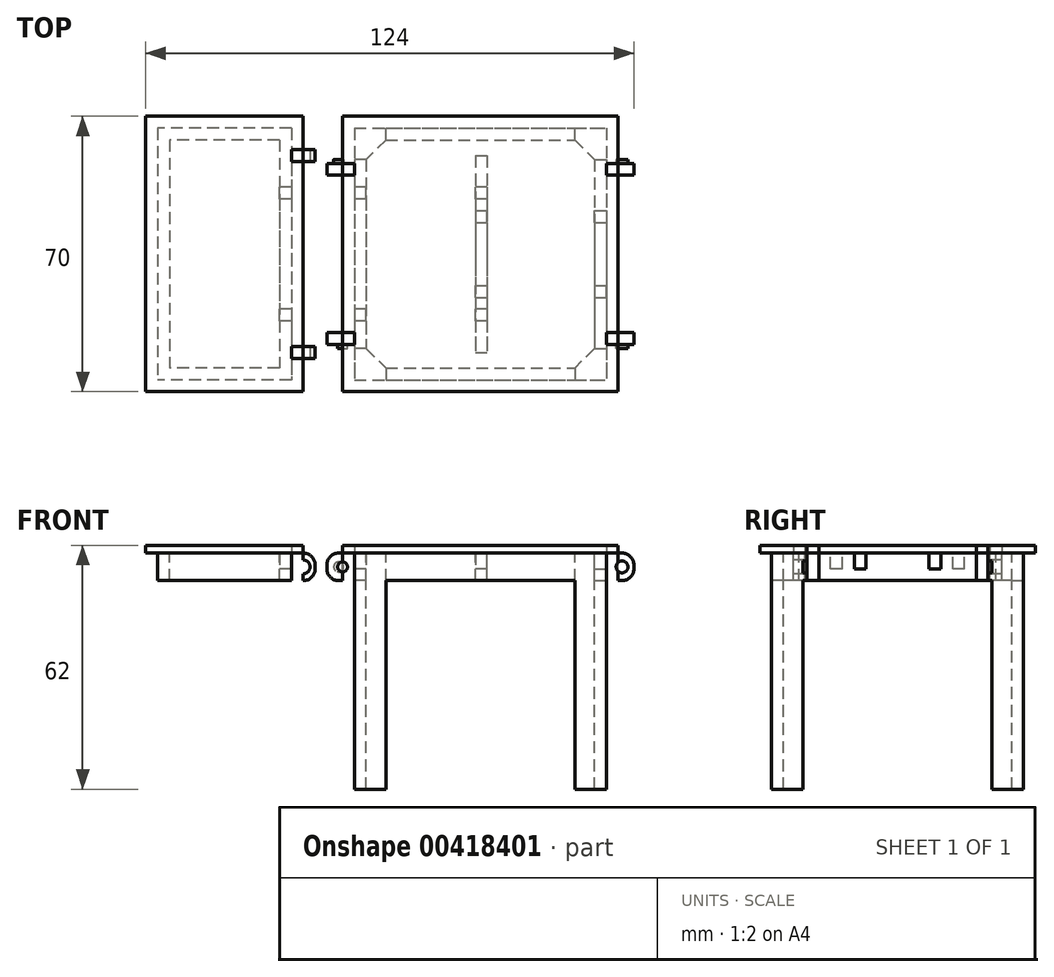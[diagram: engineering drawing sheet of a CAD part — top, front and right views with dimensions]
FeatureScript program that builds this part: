
annotation { "Feature Type Name" : "Feature", "Feature Type Description" : "" }
export const myFeature = defineFeature(function(context is Context, id is Id, definition is map)
    precondition{}
    {
        {
            var Q0;
            Q0=qCreatedBy(makeId("Top.planeOp"),FACE);
            var sketch = newSketch(context, id + "F0", { "sketchPlane" : qUnion([Q0])});
            skLineSegment(sketch, "E0.bottom", {"start": v(0, 0) * mm, "end": v(70, 0) * mm});
            skLineSegment(sketch, "E0.top", {"start": v(0, -70) * mm, "end": v(70, -70) * mm});
            skLineSegment(sketch, "E0.left", {"start": v(0, 0) * mm, "end": v(0, -70) * mm});
            skLineSegment(sketch, "E0.right", {"start": v(70, 0) * mm, "end": v(70, -70) * mm});
            skLineSegment(sketch, "E1.bottom", {"start": v(3, -3) * mm, "end": v(67, -3) * mm});
            skLineSegment(sketch, "E1.top", {"start": v(3, -67) * mm, "end": v(67, -67) * mm});
            skLineSegment(sketch, "E1.left", {"start": v(3, -3) * mm, "end": v(3, -67) * mm});
            skLineSegment(sketch, "E1.right", {"start": v(67, -3) * mm, "end": v(67, -67) * mm});
            skLineSegment(sketch, "E2.bottom", {"start": v(11, -6) * mm, "end": v(59, -6) * mm});
            skLineSegment(sketch, "E2.top", {"start": v(11, -64) * mm, "end": v(59, -64) * mm});
            skLineSegment(sketch, "E2.left", {"start": v(6, -11) * mm, "end": v(6, -59) * mm});
            skLineSegment(sketch, "E2.right", {"start": v(64, -11) * mm, "end": v(64, -59) * mm});
            skLineSegment(sketch, "E3", {"start": v(11, -6) * mm, "end": v(6, -11) * mm});
            skLineSegment(sketch, "E4", {"start": v(59, -6) * mm, "end": v(64, -11) * mm});
            skLineSegment(sketch, "E5", {"start": v(64, -59) * mm, "end": v(59, -64) * mm});
            skLineSegment(sketch, "E6", {"start": v(6, -59) * mm, "end": v(11, -64) * mm});
            skLineSegment(sketch, "E7", {"start": v(11, -6) * mm, "end": v(11, -3) * mm});
            skLineSegment(sketch, "E8", {"start": v(6, -11) * mm, "end": v(3, -11) * mm});
            skLineSegment(sketch, "E9", {"start": v(11, -64) * mm, "end": v(11, -67) * mm});
            skLineSegment(sketch, "E10", {"start": v(6, -59) * mm, "end": v(3, -59) * mm});
            skLineSegment(sketch, "E11", {"start": v(59, -64) * mm, "end": v(59, -67) * mm});
            skLineSegment(sketch, "E12", {"start": v(64, -59) * mm, "end": v(67, -59) * mm});
            skLineSegment(sketch, "E13", {"start": v(59, -6) * mm, "end": v(59, -3) * mm});
            skLineSegment(sketch, "E14", {"start": v(64, -11) * mm, "end": v(67, -11) * mm});
            skPoint(sketch, "E15.orphan", {"position": v(6, -6) * mm});
            skPoint(sketch, "E16.orphan", {"position": v(6, -64) * mm});
            skPoint(sketch, "E17.orphan", {"position": v(64, -64) * mm});
            skPoint(sketch, "E18.orphan", {"position": v(64, -6) * mm});
            skLineSegment(sketch, "E19.bottom", {"start": v(67, -12) * mm, "end": v(74, -12) * mm});
            skLineSegment(sketch, "E19.top", {"start": v(67, -15) * mm, "end": v(74, -15) * mm});
            skLineSegment(sketch, "E19.left", {"start": v(67, -12) * mm, "end": v(67, -15) * mm});
            skLineSegment(sketch, "E19.right", {"start": v(74, -12) * mm, "end": v(74, -15) * mm});
            skLineSegment(sketch, "E20.bottom", {"start": v(67, -58) * mm, "end": v(74, -58) * mm});
            skLineSegment(sketch, "E20.top", {"start": v(67, -55) * mm, "end": v(74, -55) * mm});
            skLineSegment(sketch, "E20.left", {"start": v(67, -58) * mm, "end": v(67, -55) * mm});
            skLineSegment(sketch, "E20.right", {"start": v(74, -58) * mm, "end": v(74, -55) * mm});
            skLineSegment(sketch, "E21.bottom", {"start": v(3, -12) * mm, "end": v(-4, -12) * mm});
            skLineSegment(sketch, "E21.top", {"start": v(3, -15) * mm, "end": v(-4, -15) * mm});
            skLineSegment(sketch, "E21.left", {"start": v(3, -12) * mm, "end": v(3, -15) * mm});
            skLineSegment(sketch, "E21.right", {"start": v(-4, -12) * mm, "end": v(-4, -15) * mm});
            skLineSegment(sketch, "E22.bottom", {"start": v(3, -58) * mm, "end": v(-4, -58) * mm});
            skLineSegment(sketch, "E22.top", {"start": v(3, -55) * mm, "end": v(-4, -55) * mm});
            skLineSegment(sketch, "E22.left", {"start": v(3, -58) * mm, "end": v(3, -55) * mm});
            skLineSegment(sketch, "E22.right", {"start": v(-4, -58) * mm, "end": v(-4, -55) * mm});
            skLineSegment(sketch, "E23.bottom", {"start": v(33.75, -10) * mm, "end": v(36.75, -10) * mm});
            skLineSegment(sketch, "E23.top", {"start": v(33.75, -60) * mm, "end": v(36.75, -60) * mm});
            skLineSegment(sketch, "E23.left", {"start": v(33.75, -10) * mm, "end": v(33.75, -60) * mm});
            skLineSegment(sketch, "E23.right", {"start": v(36.75, -10) * mm, "end": v(36.75, -60) * mm});
            skSolve(sketch);
        }
        {
            var Q0;
            Q0=makeQuery(id+"F0.imprint","IMPRINT",FACE,{"disambiguationData":[TD([[makeQuery(id+"F0.imprint","IMPRINT",EDGE,{"derivedFrom":sQuery(id+"F0.wireOp",EDGE,"E2.bottom")}),-1.0]])]});
            var Q1;
            Q1=makeQuery(id+"F0.imprint","IMPRINT",FACE,{"disambiguationData":[TD([[makeQuery(id+"F0.imprint","IMPRINT",EDGE,{"derivedFrom":sQuery(id+"F0.wireOp",EDGE,"E2.right")}),1.0]])]});
            var Q2;
            {var subQ14=sQuery(id+"F0.wireOp",EDGE,"E0.bottom");Q2=makeQuery(id+"F0.imprint","IMPRINT",FACE,{"disambiguationData":[TD([[makeQuery(id+"F0.imprint","IMPRINT",EDGE,{"derivedFrom":subQ14}),-1.0]])]});}
            var Q3;
            Q3=makeQuery(id+"F0.imprint","IMPRINT",FACE,{"disambiguationData":[TD([[makeQuery(id+"F0.imprint","IMPRINT",EDGE,{"derivedFrom":sQuery(id+"F0.wireOp",EDGE,"E2.left")}),-1.0]])]});
            var Q4;
            Q4=makeQuery(id+"F0.imprint","IMPRINT",FACE,{"disambiguationData":[TD([[makeQuery(id+"F0.imprint","IMPRINT",EDGE,{"derivedFrom":sQuery(id+"F0.wireOp",EDGE,"E2.top")}),-1.0]])]});
            var Q5;
            Q5=makeQuery(id+"F0.imprint","IMPRINT",FACE,{"disambiguationData":[TD([[makeQuery(id+"F0.imprint","IMPRINT",EDGE,{"derivedFrom":sQuery(id+"F0.wireOp",EDGE,"E5")}),1.0]])]});
            var Q6;
            Q6=makeQuery(id+"F0.imprint","IMPRINT",FACE,{"disambiguationData":[TD([[makeQuery(id+"F0.imprint","IMPRINT",EDGE,{"derivedFrom":sQuery(id+"F0.wireOp",EDGE,"E6")}),-1.0]])]});
            var Q7;
            Q7=makeQuery(id+"F0.imprint","IMPRINT",FACE,{"disambiguationData":[TD([[makeQuery(id+"F0.imprint","IMPRINT",EDGE,{"derivedFrom":sQuery(id+"F0.wireOp",EDGE,"E4")}),1.0]])]});
            var Q8;
            Q8=makeQuery(id+"F0.imprint","IMPRINT",FACE,{"disambiguationData":[TD([[makeQuery(id+"F0.imprint","IMPRINT",EDGE,{"derivedFrom":sQuery(id+"F0.wireOp",EDGE,"E2.bottom")}),1.0]])]});
            var Q9;
            Q9=makeQuery(id+"F0.imprint","IMPRINT",FACE,{"disambiguationData":[TD([[makeQuery(id+"F0.imprint","IMPRINT",EDGE,{"derivedFrom":sQuery(id+"F0.wireOp",EDGE,"E3")}),-1.0]])]});
            var Q10;
            {var subQ0=sQuery(id+"F0.wireOp",EDGE,"E19.top");var subQ1=sQuery(id+"F0.wireOp",EDGE,"E0.right");var subQ2=makeQuery(id+"F0.imprint","INTERSECT",VERTEX,{"derivedFrom":[subQ1,subQ0]});Q10=makeQuery(id+"F0.imprint","IMPRINT",FACE,{"disambiguationData":[TD([[makeQuery(id+"F0.imprint","IMPRINT",EDGE,{"disambiguationData":[TD([[subQ2,-1.0]])],"derivedFrom":subQ1}),-1.0]])]});}
            var Q11;
            {var subQ5=sQuery(id+"F0.wireOp",EDGE,"E19.left");Q11=makeQuery(id+"F0.imprint","IMPRINT",FACE,{"disambiguationData":[TD([[makeQuery(id+"F0.imprint","IMPRINT",EDGE,{"derivedFrom":subQ5}),1.0]])]});}
            var Q12;
            {var subQ5=sQuery(id+"F0.wireOp",EDGE,"E20.left");Q12=makeQuery(id+"F0.imprint","IMPRINT",FACE,{"disambiguationData":[TD([[makeQuery(id+"F0.imprint","IMPRINT",EDGE,{"derivedFrom":subQ5}),-1.0]])]});}
            var Q13;
            {var subQ16=sQuery(id+"F0.wireOp",EDGE,"E0.top");Q13=makeQuery(id+"F0.imprint","IMPRINT",FACE,{"disambiguationData":[TD([[makeQuery(id+"F0.imprint","IMPRINT",EDGE,{"derivedFrom":subQ16}),1.0]])]});}
            var Q14;
            {var subQ0=sQuery(id+"F0.wireOp",EDGE,"E21.top");var subQ1=sQuery(id+"F0.wireOp",EDGE,"E0.left");var subQ2=makeQuery(id+"F0.imprint","INTERSECT",VERTEX,{"derivedFrom":[subQ1,subQ0]});Q14=makeQuery(id+"F0.imprint","IMPRINT",FACE,{"disambiguationData":[TD([[makeQuery(id+"F0.imprint","IMPRINT",EDGE,{"disambiguationData":[TD([[subQ2,-1.0]])],"derivedFrom":subQ1}),1.0]])]});}
            var Q15;
            {var subQ5=sQuery(id+"F0.wireOp",EDGE,"E22.left");Q15=makeQuery(id+"F0.imprint","IMPRINT",FACE,{"disambiguationData":[TD([[makeQuery(id+"F0.imprint","IMPRINT",EDGE,{"derivedFrom":subQ5}),1.0]])]});}
            var Q16;
            {var subQ5=sQuery(id+"F0.wireOp",EDGE,"E21.left");Q16=makeQuery(id+"F0.imprint","IMPRINT",FACE,{"disambiguationData":[TD([[makeQuery(id+"F0.imprint","IMPRINT",EDGE,{"derivedFrom":subQ5}),-1.0]])]});}
            var Q17;
            Q17=makeQuery(id+"F0.imprint","IMPRINT",FACE,{"disambiguationData":[TD([[makeQuery(id+"F0.imprint","IMPRINT",EDGE,{"derivedFrom":sQuery(id+"F0.wireOp",EDGE,"E23.bottom")}),-1.0]])]});
            extrude(context, id + "F1", {"entities" : qUnion([Q0, Q1, Q2, Q3, Q4, Q5, Q6, Q7, Q8, Q9, Q10, Q11, Q12, Q13, Q14, Q15, Q16, Q17]), "depth" : 2 * mm});
        }
        {
            var Q0;
            Q0=makeQuery(id+"F0.imprint","IMPRINT",FACE,{"disambiguationData":[TD([[makeQuery(id+"F0.imprint","IMPRINT",EDGE,{"derivedFrom":sQuery(id+"F0.wireOp",EDGE,"E5")}),1.0]])]});
            var Q1;
            Q1=makeQuery(id+"F0.imprint","IMPRINT",FACE,{"disambiguationData":[TD([[makeQuery(id+"F0.imprint","IMPRINT",EDGE,{"derivedFrom":sQuery(id+"F0.wireOp",EDGE,"E4")}),1.0]])]});
            var Q2;
            Q2=makeQuery(id+"F0.imprint","IMPRINT",FACE,{"disambiguationData":[TD([[makeQuery(id+"F0.imprint","IMPRINT",EDGE,{"derivedFrom":sQuery(id+"F0.wireOp",EDGE,"E3")}),-1.0]])]});
            var Q3;
            Q3=makeQuery(id+"F0.imprint","IMPRINT",FACE,{"disambiguationData":[TD([[makeQuery(id+"F0.imprint","IMPRINT",EDGE,{"derivedFrom":sQuery(id+"F0.wireOp",EDGE,"E6")}),-1.0]])]});
            extrude(context, id + "F2", {"entities" : qUnion([Q0, Q1, Q2, Q3]), "operationType" : NewBodyOperationType.ADD, "oppositeDirection" : true, "depth" : 60 * mm});
        }
        {
            var Q0;
            Q0=makeQuery(id+"F0.imprint","IMPRINT",FACE,{"disambiguationData":[TD([[makeQuery(id+"F0.imprint","IMPRINT",EDGE,{"derivedFrom":sQuery(id+"F0.wireOp",EDGE,"E2.left")}),-1.0]])]});
            var Q1;
            {var subQ5=sQuery(id+"F0.wireOp",EDGE,"E22.right");Q1=makeQuery(id+"F0.imprint","IMPRINT",FACE,{"disambiguationData":[TD([[makeQuery(id+"F0.imprint","IMPRINT",EDGE,{"derivedFrom":subQ5}),-1.0]])]});}
            var Q2;
            {var subQ5=sQuery(id+"F0.wireOp",EDGE,"E22.left");Q2=makeQuery(id+"F0.imprint","IMPRINT",FACE,{"disambiguationData":[TD([[makeQuery(id+"F0.imprint","IMPRINT",EDGE,{"derivedFrom":subQ5}),1.0]])]});}
            var Q3;
            {var subQ5=sQuery(id+"F0.wireOp",EDGE,"E21.left");Q3=makeQuery(id+"F0.imprint","IMPRINT",FACE,{"disambiguationData":[TD([[makeQuery(id+"F0.imprint","IMPRINT",EDGE,{"derivedFrom":subQ5}),-1.0]])]});}
            var Q4;
            {var subQ5=sQuery(id+"F0.wireOp",EDGE,"E21.right");Q4=makeQuery(id+"F0.imprint","IMPRINT",FACE,{"disambiguationData":[TD([[makeQuery(id+"F0.imprint","IMPRINT",EDGE,{"derivedFrom":subQ5}),1.0]])]});}
            var Q5;
            Q5=makeQuery(id+"F0.imprint","IMPRINT",FACE,{"disambiguationData":[TD([[makeQuery(id+"F0.imprint","IMPRINT",EDGE,{"derivedFrom":sQuery(id+"F0.wireOp",EDGE,"E2.top")}),-1.0]])]});
            var Q6;
            Q6=makeQuery(id+"F0.imprint","IMPRINT",FACE,{"disambiguationData":[TD([[makeQuery(id+"F0.imprint","IMPRINT",EDGE,{"derivedFrom":sQuery(id+"F0.wireOp",EDGE,"E2.right")}),1.0]])]});
            var Q7;
            {var subQ5=sQuery(id+"F0.wireOp",EDGE,"E20.left");Q7=makeQuery(id+"F0.imprint","IMPRINT",FACE,{"disambiguationData":[TD([[makeQuery(id+"F0.imprint","IMPRINT",EDGE,{"derivedFrom":subQ5}),-1.0]])]});}
            var Q8;
            {var subQ5=sQuery(id+"F0.wireOp",EDGE,"E20.right");Q8=makeQuery(id+"F0.imprint","IMPRINT",FACE,{"disambiguationData":[TD([[makeQuery(id+"F0.imprint","IMPRINT",EDGE,{"derivedFrom":subQ5}),1.0]])]});}
            var Q9;
            {var subQ5=sQuery(id+"F0.wireOp",EDGE,"E19.right");Q9=makeQuery(id+"F0.imprint","IMPRINT",FACE,{"disambiguationData":[TD([[makeQuery(id+"F0.imprint","IMPRINT",EDGE,{"derivedFrom":subQ5}),-1.0]])]});}
            var Q10;
            {var subQ5=sQuery(id+"F0.wireOp",EDGE,"E19.left");Q10=makeQuery(id+"F0.imprint","IMPRINT",FACE,{"disambiguationData":[TD([[makeQuery(id+"F0.imprint","IMPRINT",EDGE,{"derivedFrom":subQ5}),1.0]])]});}
            var Q11;
            Q11=makeQuery(id+"F0.imprint","IMPRINT",FACE,{"disambiguationData":[TD([[makeQuery(id+"F0.imprint","IMPRINT",EDGE,{"derivedFrom":sQuery(id+"F0.wireOp",EDGE,"E2.bottom")}),1.0]])]});
            var Q12;
            Q12=makeQuery(id+"F0.imprint","IMPRINT",FACE,{"disambiguationData":[TD([[makeQuery(id+"F0.imprint","IMPRINT",EDGE,{"derivedFrom":sQuery(id+"F0.wireOp",EDGE,"E23.bottom")}),-1.0]])]});
            extrude(context, id + "F3", {"entities" : qUnion([Q0, Q1, Q2, Q3, Q4, Q5, Q6, Q7, Q8, Q9, Q10, Q11, Q12]), "operationType" : NewBodyOperationType.ADD, "oppositeDirection" : true, "depth" : 7 * mm});
        }
        {
            var Q0;
            Q0=makeQuery(id+"F3.opExtrude","SWEPT_FACE",FACE,{"disambiguationData":[OSD([sQuery(id+"F0.wireOp",EDGE,"E21.bottom")])]});
            var sketch = newSketch(context, id + "F4", { "sketchPlane" : qUnion([Q0])});
            skCircle(sketch, "E24", {"center": v(1, -3.5) * mm, "radius": 1.25 * mm});
            skCircle(sketch, "E25", {"center": v(-71, -3.5) * mm, "radius": 1.5 * mm});
            skSolve(sketch);
        }
        {
            var Q0;
            Q0=makeQuery(id+"F4.imprint","IMPRINT",FACE,{"disambiguationData":[TD([[makeQuery(id+"F4.imprint","IMPRINT",EDGE,{"derivedFrom":sQuery(id+"F4.wireOp",EDGE,"E24")}),1.0]])]});
            var Q1;
            Q1=makeQuery(id+"F4.imprint","IMPRINT",FACE,{"disambiguationData":[TD([[makeQuery(id+"F4.imprint","IMPRINT",EDGE,{"derivedFrom":sQuery(id+"F4.wireOp",EDGE,"E25")}),1.0]])]});
            extrude(context, id + "F5", {"entities" : qUnion([Q0, Q1]), "operationType" : NewBodyOperationType.ADD, "depth" : 1 * mm});
        }
        {
            var Q0;
            Q0=makeQuery(id+"F3.opExtrude","SWEPT_FACE",FACE,{"disambiguationData":[OSD([sQuery(id+"F0.wireOp",EDGE,"E22.bottom")])]});
            var sketch = newSketch(context, id + "F6", { "sketchPlane" : qUnion([Q0])});
            skCircle(sketch, "E26", {"center": v(0, -3.5) * mm, "radius": 1.25 * mm});
            skCircle(sketch, "E27", {"center": v(71, -3.5) * mm, "radius": 1.5 * mm});
            skSolve(sketch);
        }
        {
            var Q0;
            Q0=makeQuery(id+"F6.imprint","IMPRINT",FACE,{"disambiguationData":[TD([[makeQuery(id+"F6.imprint","IMPRINT",EDGE,{"derivedFrom":sQuery(id+"F6.wireOp",EDGE,"E26")}),1.0]])]});
            var Q1;
            Q1=makeQuery(id+"F6.imprint","IMPRINT",FACE,{"disambiguationData":[TD([[makeQuery(id+"F6.imprint","IMPRINT",EDGE,{"derivedFrom":sQuery(id+"F6.wireOp",EDGE,"E27")}),1.0]])]});
            extrude(context, id + "F7", {"entities" : qUnion([Q0, Q1]), "operationType" : NewBodyOperationType.ADD, "depth" : 1 * mm});
        }
        {
            var Q0;
            Q0=qCreatedBy(makeId("Top.planeOp"),FACE);
            var sketch = newSketch(context, id + "F8", { "sketchPlane" : qUnion([Q0])});
            skLineSegment(sketch, "E28.bottom", {"start": v(-10, 0) * mm, "end": v(-50, 0) * mm});
            skLineSegment(sketch, "E28.top", {"start": v(-10, -70) * mm, "end": v(-50, -70) * mm});
            skLineSegment(sketch, "E28.left", {"start": v(-10, 0) * mm, "end": v(-10, -70) * mm});
            skLineSegment(sketch, "E28.right", {"start": v(-50, 0) * mm, "end": v(-50, -70) * mm});
            skLineSegment(sketch, "E29.0", {"start": v(-13, -3) * mm, "end": v(-47, -3) * mm});
            skLineSegment(sketch, "E29.1", {"start": v(-13, -3) * mm, "end": v(-13, -67) * mm});
            skLineSegment(sketch, "E29.2", {"start": v(-13, -67) * mm, "end": v(-47, -67) * mm});
            skLineSegment(sketch, "E29.3", {"start": v(-47, -3) * mm, "end": v(-47, -67) * mm});
            skLineSegment(sketch, "E30.0", {"start": v(-44, -6) * mm, "end": v(-44, -64) * mm});
            skLineSegment(sketch, "E30.1", {"start": v(-16, -6) * mm, "end": v(-44, -6) * mm});
            skLineSegment(sketch, "E30.2", {"start": v(-16, -6) * mm, "end": v(-16, -64) * mm});
            skLineSegment(sketch, "E30.3", {"start": v(-16, -64) * mm, "end": v(-44, -64) * mm});
            skLineSegment(sketch, "E31.bottom", {"start": v(-13, -11.5) * mm, "end": v(-7, -11.5) * mm});
            skLineSegment(sketch, "E31.top", {"start": v(-13, -8.5) * mm, "end": v(-7, -8.5) * mm});
            skLineSegment(sketch, "E31.left", {"start": v(-13, -11.5) * mm, "end": v(-13, -8.5) * mm});
            skLineSegment(sketch, "E31.right", {"start": v(-7, -11.5) * mm, "end": v(-7, -8.5) * mm});
            skLineSegment(sketch, "E32.bottom", {"start": v(-13, -58.5) * mm, "end": v(-7, -58.5) * mm});
            skLineSegment(sketch, "E32.top", {"start": v(-13, -61.5) * mm, "end": v(-7, -61.5) * mm});
            skLineSegment(sketch, "E32.left", {"start": v(-13, -58.5) * mm, "end": v(-13, -61.5) * mm});
            skLineSegment(sketch, "E32.right", {"start": v(-7, -58.5) * mm, "end": v(-7, -61.5) * mm});
            skSolve(sketch);
        }
        {
            var Q0;
            Q0=makeQuery(id+"F8.imprint","IMPRINT",FACE,{"disambiguationData":[TD([[makeQuery(id+"F8.imprint","IMPRINT",EDGE,{"derivedFrom":sQuery(id+"F8.wireOp",EDGE,"E30.0")}),1.0]])]});
            var Q1;
            {var subQ7=sQuery(id+"F8.wireOp",EDGE,"E28.bottom");Q1=makeQuery(id+"F8.imprint","IMPRINT",FACE,{"disambiguationData":[TD([[makeQuery(id+"F8.imprint","IMPRINT",EDGE,{"derivedFrom":subQ7}),1.0]])]});}
            var Q2;
            {var subQ1=sQuery(id+"F8.wireOp",EDGE,"E29.0");Q2=makeQuery(id+"F8.imprint","IMPRINT",FACE,{"disambiguationData":[TD([[makeQuery(id+"F8.imprint","IMPRINT",EDGE,{"derivedFrom":subQ1}),1.0]])]});}
            var Q3;
            {var subQ0=sQuery(id+"F8.wireOp",EDGE,"E31.bottom");var subQ1=sQuery(id+"F8.wireOp",EDGE,"E28.left");var subQ2=makeQuery(id+"F8.imprint","INTERSECT",VERTEX,{"derivedFrom":[subQ1,subQ0]});Q3=makeQuery(id+"F8.imprint","IMPRINT",FACE,{"disambiguationData":[TD([[makeQuery(id+"F8.imprint","IMPRINT",EDGE,{"disambiguationData":[TD([[subQ2,-1.0]])],"derivedFrom":subQ1}),-1.0]])]});}
            var Q4;
            {var subQ5=sQuery(id+"F8.wireOp",EDGE,"E32.left");Q4=makeQuery(id+"F8.imprint","IMPRINT",FACE,{"disambiguationData":[TD([[makeQuery(id+"F8.imprint","IMPRINT",EDGE,{"derivedFrom":subQ5}),1.0]])]});}
            var Q5;
            {var subQ5=sQuery(id+"F8.wireOp",EDGE,"E31.left");Q5=makeQuery(id+"F8.imprint","IMPRINT",FACE,{"disambiguationData":[TD([[makeQuery(id+"F8.imprint","IMPRINT",EDGE,{"derivedFrom":subQ5}),-1.0]])]});}
            extrude(context, id + "F9", {"entities" : qUnion([Q0, Q1, Q2, Q3, Q4, Q5]), "depth" : 2 * mm});
        }
        {
            var Q0;
            {var subQ1=sQuery(id+"F8.wireOp",EDGE,"E29.0");Q0=makeQuery(id+"F8.imprint","IMPRINT",FACE,{"disambiguationData":[TD([[makeQuery(id+"F8.imprint","IMPRINT",EDGE,{"derivedFrom":subQ1}),1.0]])]});}
            extrude(context, id + "F10", {"entities" : qUnion([Q0]), "operationType" : NewBodyOperationType.ADD, "oppositeDirection" : true, "depth" : 7 * mm});
        }
        {
            var Q0;
            {var subQ5=sQuery(id+"F8.wireOp",EDGE,"E32.left");Q0=makeQuery(id+"F8.imprint","IMPRINT",FACE,{"disambiguationData":[TD([[makeQuery(id+"F8.imprint","IMPRINT",EDGE,{"derivedFrom":subQ5}),1.0]])]});}
            var Q1;
            {var subQ5=sQuery(id+"F8.wireOp",EDGE,"E32.right");Q1=makeQuery(id+"F8.imprint","IMPRINT",FACE,{"disambiguationData":[TD([[makeQuery(id+"F8.imprint","IMPRINT",EDGE,{"derivedFrom":subQ5}),-1.0]])]});}
            var Q2;
            {var subQ5=sQuery(id+"F8.wireOp",EDGE,"E31.right");Q2=makeQuery(id+"F8.imprint","IMPRINT",FACE,{"disambiguationData":[TD([[makeQuery(id+"F8.imprint","IMPRINT",EDGE,{"derivedFrom":subQ5}),1.0]])]});}
            var Q3;
            {var subQ5=sQuery(id+"F8.wireOp",EDGE,"E31.left");Q3=makeQuery(id+"F8.imprint","IMPRINT",FACE,{"disambiguationData":[TD([[makeQuery(id+"F8.imprint","IMPRINT",EDGE,{"derivedFrom":subQ5}),-1.0]])]});}
            extrude(context, id + "F11", {"entities" : qUnion([Q0, Q1, Q2, Q3]), "operationType" : NewBodyOperationType.ADD, "oppositeDirection" : true, "depth" : 7 * mm});
        }
        {
            var Q0;
            Q0=makeQuery(id+"F11.opExtrude","SWEPT_FACE",FACE,{"disambiguationData":[OSD([sQuery(id+"F8.wireOp",EDGE,"E32.top")])]});
            var sketch = newSketch(context, id + "F12", { "sketchPlane" : qUnion([Q0])});
            skCircle(sketch, "E33", {"center": v(-10, -3.5) * mm, "radius": 1.75 * mm});
            skSolve(sketch);
        }
        {
            var Q0;
            Q0=makeQuery(id+"F12.imprint","IMPRINT",FACE,{"disambiguationData":[TD([[makeQuery(id+"F12.imprint","IMPRINT",EDGE,{"derivedFrom":sQuery(id+"F12.wireOp",EDGE,"E33")}),1.0]])]});
            extrude(context, id + "F13", {"entities" : qUnion([Q0]), "operationType" : NewBodyOperationType.REMOVE, "endBound" : BoundingType.THROUGH_ALL, "oppositeDirection" : true, "depth" : 25 * mm});
        }
        {
            var Q0;
            Q0=makeQuery(id+"F10.opExtrude","SWEPT_FACE",FACE,{"disambiguationData":[OSD([sQuery(id+"F8.wireOp",EDGE,"E30.2")])]});
            var sketch = newSketch(context, id + "F14", { "sketchPlane" : qUnion([Q0])});
            skLineSegment(sketch, "E34.bottom", {"start": v(21, 0) * mm, "end": v(18, 0) * mm});
            skLineSegment(sketch, "E34.top", {"start": v(21, -4) * mm, "end": v(18, -4) * mm});
            skLineSegment(sketch, "E34.left", {"start": v(21, 0) * mm, "end": v(21, -4) * mm});
            skLineSegment(sketch, "E34.right", {"start": v(18, 0) * mm, "end": v(18, -4) * mm});
            skLineSegment(sketch, "E35.bottom", {"start": v(52, 0) * mm, "end": v(49, 0) * mm});
            skLineSegment(sketch, "E35.top", {"start": v(52, -4) * mm, "end": v(49, -4) * mm});
            skLineSegment(sketch, "E35.left", {"start": v(52, 0) * mm, "end": v(52, -4) * mm});
            skLineSegment(sketch, "E35.right", {"start": v(49, 0) * mm, "end": v(49, -4) * mm});
            skSolve(sketch);
        }
        {
            var Q0;
            Q0=makeQuery(id+"F14.imprint","IMPRINT",FACE,{"disambiguationData":[TD([[makeQuery(id+"F14.imprint","IMPRINT",EDGE,{"derivedFrom":sQuery(id+"F14.wireOp",EDGE,"E35.bottom")}),-1.0]])]});
            var Q1;
            Q1=makeQuery(id+"F14.imprint","IMPRINT",FACE,{"disambiguationData":[TD([[makeQuery(id+"F14.imprint","IMPRINT",EDGE,{"derivedFrom":sQuery(id+"F14.wireOp",EDGE,"E34.bottom")}),-1.0]])]});
            var Q2;
            Q2=makeQuery(id+"F3.opExtrude","SWEPT_FACE",FACE,{"disambiguationData":[OSD([sQuery(id+"F0.wireOp",EDGE,"E23.right")])]});
            extrude(context, id + "F15", {"entities" : qUnion([Q0, Q1]), "operationType" : NewBodyOperationType.REMOVE, "endBound" : BoundingType.UP_TO_SURFACE, "oppositeDirection" : true, "endBoundEntityFace" : qUnion([Q2]), "depth" : 25 * mm});
        }
        {
            var Q0;
            Q0=makeQuery(id+"F11.opExtrude","CAP_EDGE",EDGE,{"disambiguationData":[OSD([sQuery(id+"F8.wireOp",EDGE,"E31.right")])],"isStart":false});
            var Q1;
            Q1=makeQuery(id+"F3.opExtrude","CAP_EDGE",EDGE,{"disambiguationData":[OSD([sQuery(id+"F0.wireOp",EDGE,"E21.right")])],"isStart":false});
            var Q2;
            Q2=makeQuery(id+"F11.opExtrude","CAP_EDGE",EDGE,{"disambiguationData":[OSD([sQuery(id+"F8.wireOp",EDGE,"E32.right")])],"isStart":false});
            var Q3;
            Q3=makeQuery(id+"F3.opExtrude","CAP_EDGE",EDGE,{"disambiguationData":[OSD([sQuery(id+"F0.wireOp",EDGE,"E22.right")])],"isStart":false});
            var Q4;
            Q4=makeQuery(id+"F3.opExtrude","CAP_EDGE",EDGE,{"disambiguationData":[OSD([sQuery(id+"F0.wireOp",EDGE,"E19.right")])],"isStart":false});
            var Q5;
            Q5=makeQuery(id+"F3.opExtrude","CAP_EDGE",EDGE,{"disambiguationData":[OSD([sQuery(id+"F0.wireOp",EDGE,"E20.right")])],"isStart":false});
            fillet(context, id + "F16", {"entities" : qUnion([Q0, Q1, Q2, Q3, Q4, Q5]), "radius" : 3 * mm, "tangentPropagation" : true, "allowEdgeOverflow" : false});
        }
        {
            var Q0;
            Q0=makeQuery(id+"F3.opExtrude","CAP_EDGE",EDGE,{"disambiguationData":[OSD([sQuery(id+"F0.wireOp",EDGE,"E21.right")])],"isStart":true});
            var Q1;
            Q1=makeQuery(id+"F3.opExtrude","CAP_EDGE",EDGE,{"disambiguationData":[OSD([sQuery(id+"F0.wireOp",EDGE,"E22.right")])],"isStart":true});
            var Q2;
            Q2=makeQuery(id+"F11.opExtrude","CAP_EDGE",EDGE,{"disambiguationData":[OSD([sQuery(id+"F8.wireOp",EDGE,"E32.right")])],"isStart":true});
            var Q3;
            Q3=makeQuery(id+"F11.opExtrude","CAP_EDGE",EDGE,{"disambiguationData":[OSD([sQuery(id+"F8.wireOp",EDGE,"E31.right")])],"isStart":true});
            var Q4;
            Q4=makeQuery(id+"F3.opExtrude","CAP_EDGE",EDGE,{"disambiguationData":[OSD([sQuery(id+"F0.wireOp",EDGE,"E19.right")])],"isStart":true});
            var Q5;
            Q5=makeQuery(id+"F3.opExtrude","CAP_EDGE",EDGE,{"disambiguationData":[OSD([sQuery(id+"F0.wireOp",EDGE,"E20.right")])],"isStart":true});
            fillet(context, id + "F17", {"entities" : qUnion([Q0, Q1, Q2, Q3, Q4, Q5]), "radius" : 3 * mm, "tangentPropagation" : true, "allowEdgeOverflow" : false});
        }
        {
            var Q0;
            {var subQ0=sQuery(id+"F0.wireOp",EDGE,"E1.right");Q0=makeQuery(id+"F3.opExtrude","SWEPT_FACE",FACE,{"disambiguationData":[OSD([subQ0]),TDD([makeQuery(id+"F0.imprint","IMPRINT",EDGE,{"disambiguationData":[TD([[makeQuery(id+"F0.imprint","INTERSECT",VERTEX,{"derivedFrom":[subQ0,sQuery(id+"F0.wireOp",EDGE,"E19.top"),sQuery(id+"F0.wireOp",EDGE,"E19.left")]}),-1.0]])],"derivedFrom":subQ0})])]});}
            var sketch = newSketch(context, id + "F18", { "sketchPlane" : qUnion([Q0])});
            skLineSegment(sketch, "E36.bottom", {"start": v(-46, 0) * mm, "end": v(-43, 0) * mm});
            skLineSegment(sketch, "E36.top", {"start": v(-46, -4) * mm, "end": v(-43, -4) * mm});
            skLineSegment(sketch, "E36.left", {"start": v(-46, 0) * mm, "end": v(-46, -4) * mm});
            skLineSegment(sketch, "E36.right", {"start": v(-43, 0) * mm, "end": v(-43, -4) * mm});
            skLineSegment(sketch, "E37.bottom", {"start": v(-24, 0) * mm, "end": v(-27, 0) * mm});
            skLineSegment(sketch, "E37.top", {"start": v(-24, -4) * mm, "end": v(-27, -4) * mm});
            skLineSegment(sketch, "E37.left", {"start": v(-24, 0) * mm, "end": v(-24, -4) * mm});
            skLineSegment(sketch, "E37.right", {"start": v(-27, 0) * mm, "end": v(-27, -4) * mm});
            skSolve(sketch);
        }
        {
            var Q0;
            Q0 = qSketchRegion(id + "F18", true);
            var Q1;
            Q1=makeQuery(id+"F3.opExtrude","SWEPT_FACE",FACE,{"disambiguationData":[OSD([sQuery(id+"F0.wireOp",EDGE,"E23.left")])]});
            extrude(context, id + "F19", {"entities" : qUnion([Q0]), "operationType" : NewBodyOperationType.REMOVE, "endBound" : BoundingType.UP_TO_SURFACE, "oppositeDirection" : true, "endBoundEntityFace" : qUnion([Q1]), "depth" : 25 * mm});
        }
    });
